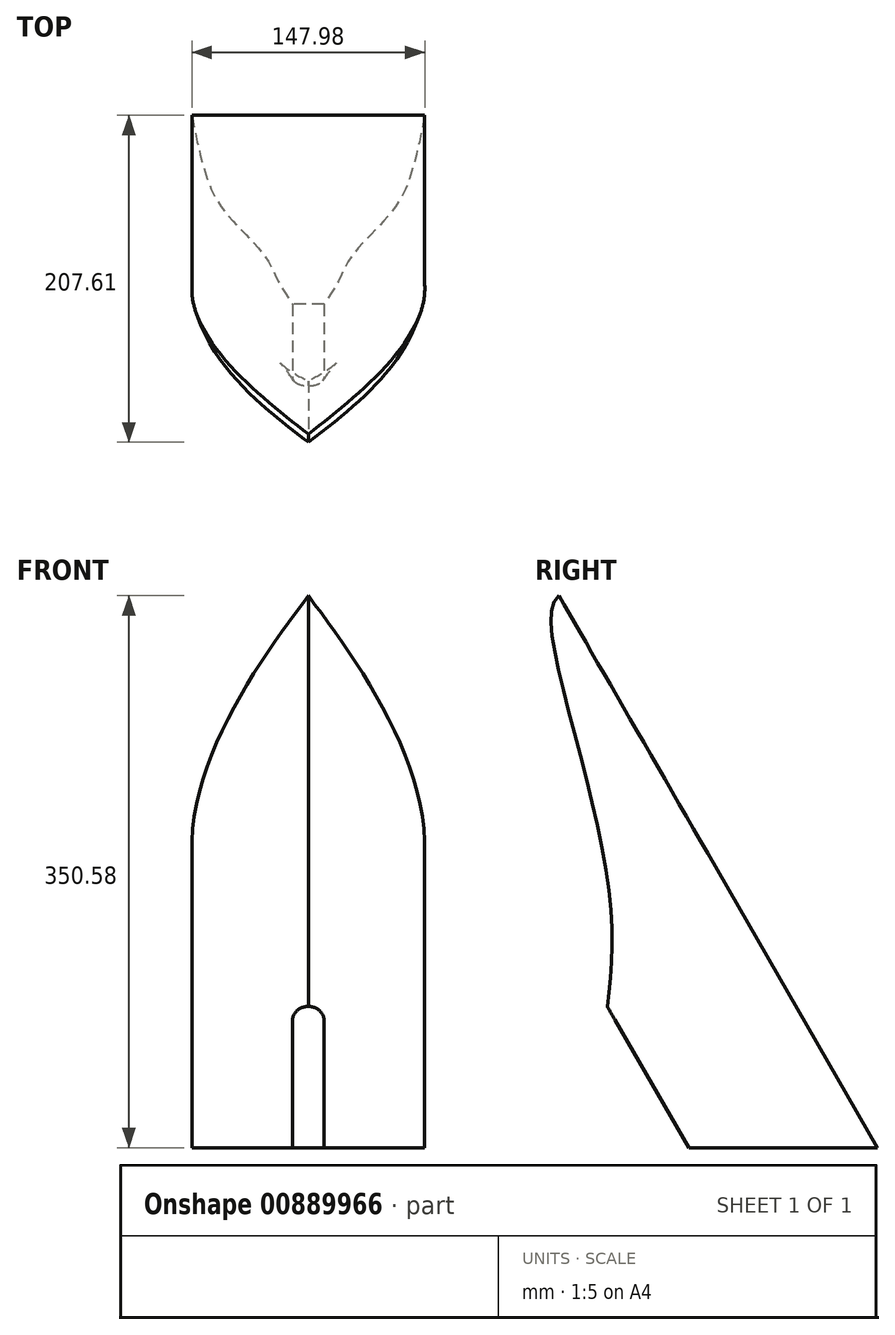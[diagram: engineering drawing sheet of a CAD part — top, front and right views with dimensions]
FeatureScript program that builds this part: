
annotation { "Feature Type Name" : "Feature", "Feature Type Description" : "" }
export const myFeature = defineFeature(function(context is Context, id is Id, definition is map)
    precondition{}
    {
        {
            var Q0;
            Q0=qCreatedBy(makeId("Top.planeOp"),FACE);
            var sketch = newSketch(context, id + "F0", { "sketchPlane" : qUnion([Q0])});
            skLineSegment(sketch, "E0", {"start": v(-73.92, 60.85) * mm, "end": v(0, 60.85) * mm});
            skPoint(sketch, "E0.startSnap0", {"position": v(0, 60.85) * mm});
            skFitSpline(sketch, "E1", {"points": [v(-73.92, 60.85) * mm, v(-60.5, 11.54) * mm, v(-42.77, -11.7) * mm, v(-25.64, -31.45) * mm, v(-18.22, -46.15) * mm, v(-9.95, -59.12) * mm], "startDerivative": vector(38.5, -196.23) * mm, "endDerivative": vector(58.27, -83.13) * mm});
            skLineSegment(sketch, "E2", {"start": v(-9.95, -59.12) * mm, "end": v(0, -59.12) * mm});
            skPoint(sketch, "E3.orphan", {"position": v(0, 0) * mm});
            skPoint(sketch, "E4.end.orphan", {"position": v(0, -90.36) * mm});
            skPoint(sketch, "E5.end.orphan", {"position": v(0, 121.7) * mm});
            skLineSegment(sketch, "E6", {"start": v(0, 100.37) * mm, "end": v(0, -90.36) * mm, "construction": true});
            skFitSpline(sketch, "E7.MirrorCS", {"points": [v(73.92, 60.85) * mm, v(60.5, 11.54) * mm, v(42.77, -11.7) * mm, v(25.64, -31.45) * mm, v(18.22, -46.15) * mm, v(9.95, -59.12) * mm], "startDerivative": vector(-38.5, -196.23) * mm, "endDerivative": vector(-58.27, -83.13) * mm});
            skLineSegment(sketch, "E8.MirrorCS", {"start": v(73.92, 60.85) * mm, "end": v(0, 60.85) * mm});
            skLineSegment(sketch, "E9.MirrorCS", {"start": v(9.95, -59.12) * mm, "end": v(0, -59.12) * mm});
            skLineSegment(sketch, "E10", {"start": v(-25.64, -31.45) * mm, "end": v(25.64, -31.45) * mm});
            skSolve(sketch);
        }
        {
            var Q0;
            Q0=sQuery(id+"F0.wireOp",EDGE,"E9.MirrorCS");
            cPlane(context, id + "F1", {"entities" : qUnion([Q0]), "cplaneType" : CPlaneType.LINE_ANGLE, "offset" : 25 * mm, "angle" : 150 * degree, "width" : 150 * mm, "height" : 150 * mm});
        }
        {
            var Q0;
            Q0=qCreatedBy(id+"F1.planeOp",FACE);
            var sketch = newSketch(context, id + "F2", { "sketchPlane" : qUnion([Q0])});
            skLineSegment(sketch, "E11.0", {"start": v(-9.95, 29.56) * mm, "end": v(0, 29.56) * mm});
            skLineSegment(sketch, "E12.0", {"start": v(9.95, 29.56) * mm, "end": v(0, 29.56) * mm});
            skLineSegment(sketch, "E13", {"start": v(-9.95, 29.56) * mm, "end": v(-9.95, 123.16) * mm});
            skLineSegment(sketch, "E14", {"start": v(9.95, 29.56) * mm, "end": v(9.95, 123.16) * mm});
            skArc(sketch, "E15", {"start": v(-9.95, 123.16) * mm, "mid": v(0, 133.11) * mm, "end": v(9.95, 123.16) * mm});
            skPoint(sketch, "E16", {"position": v(0, 133.11) * mm});
            skSolve(sketch);
        }
        {
            var Q0;
            Q0=sQuery(id+"F0.wireOp",EDGE,"E8.MirrorCS");
            cPlane(context, id + "F3", {"entities" : qUnion([Q0]), "cplaneType" : CPlaneType.LINE_ANGLE, "offset" : 25 * mm, "angle" : 150 * degree, "width" : 150 * mm, "height" : 150 * mm});
        }
        {
            var Q0;
            Q0=qCreatedBy(id+"F3.planeOp",FACE);
            var sketch = newSketch(context, id + "F4", { "sketchPlane" : qUnion([Q0])});
            skLineSegment(sketch, "E17.0", {"start": v(-73.92, -30.42) * mm, "end": v(0, -30.42) * mm});
            skLineSegment(sketch, "E18.0", {"start": v(73.92, -30.42) * mm, "end": v(0, -30.42) * mm});
            skLineSegment(sketch, "E19", {"start": v(-73.92, -30.42) * mm, "end": v(-73.92, 185.3) * mm});
            skLineSegment(sketch, "E20", {"start": v(73.92, -30.42) * mm, "end": v(73.92, 185.3) * mm});
            skFitSpline(sketch, "E21", {"points": [v(-73.92, 185.3) * mm, v(0, 374.4) * mm], "startDerivative": vector(-6.14, 208.86) * mm, "endDerivative": vector(91.46, 141.36) * mm});
            skLineSegment(sketch, "E22", {"start": v(0, -30.42) * mm, "end": v(0, 390.57) * mm, "construction": true});
            skFitSpline(sketch, "E23.MirrorCS", {"points": [v(73.92, 185.3) * mm, v(0, 374.4) * mm], "startDerivative": vector(6.14, 208.86) * mm, "endDerivative": vector(-91.46, 141.36) * mm});
            skSolve(sketch);
        }
        {
            var Q0;
            Q0=sQuery(id+"F4.wireOp",EDGE,"E22");
            cPlane(context, id + "F5", {"entities" : qUnion([Q0]), "cplaneType" : CPlaneType.LINE_ANGLE, "offset" : 25 * mm, "angle" : 0 * degree, "width" : 150 * mm, "height" : 150 * mm});
        }
        {
            var Q0;
            Q0=qCreatedBy(id+"F5.planeOp",FACE);
            var sketch = newSketch(context, id + "F6", { "sketchPlane" : qUnion([Q0])});
            skPoint(sketch, "E24.0", {"position": v(-141.56, 350.58) * mm});
            skPoint(sketch, "E25.0", {"position": v(-110.9, 89.68) * mm});
            skFitSpline(sketch, "E26", {"points": [v(-110.9, 89.68) * mm, v(-110.9, 171.43) * mm, v(-143.63, 312.22) * mm, v(-141.56, 350.58) * mm], "startDerivative": vector(28.7, 200.9) * mm, "endDerivative": vector(94.15, 70.36) * mm});
            skSolve(sketch);
        }
        {
            var Q0;
            Q0=sQuery(id+"F0.wireOp",EDGE,"E10");
            cPlane(context, id + "F7", {"entities" : qUnion([Q0]), "cplaneType" : CPlaneType.LINE_ANGLE, "offset" : 25 * mm, "angle" : 30 * degree, "width" : 150 * mm, "height" : 150 * mm});
        }
        {
            var Q0;
            Q0=qCreatedBy(id+"F7.planeOp",FACE);
            var sketch = newSketch(context, id + "F8", { "sketchPlane" : qUnion([Q0])});
            skLineSegment(sketch, "E27.0", {"start": v(25.64, 15.72) * mm, "end": v(-25.64, 15.72) * mm});
            skLineSegment(sketch, "E28", {"start": v(25.64, 15.72) * mm, "end": v(25.64, 145.02) * mm});
            skLineSegment(sketch, "E29", {"start": v(-25.64, 15.72) * mm, "end": v(-25.64, 145.02) * mm});
            skFitSpline(sketch, "E30", {"points": [v(25.64, 145.02) * mm, v(0, 168.46) * mm], "startDerivative": vector(-16.25, 29.44) * mm, "endDerivative": vector(-25.64, 22.79) * mm});
            skLineSegment(sketch, "E31", {"start": v(0, 168.46) * mm, "end": v(0, 121.19) * mm, "construction": true});
            skFitSpline(sketch, "E32.MirrorCS", {"points": [v(-25.64, 145.02) * mm, v(0, 168.46) * mm], "startDerivative": vector(16.25, 29.44) * mm, "endDerivative": vector(25.64, 22.79) * mm});
            skSolve(sketch);
        }
        {
            var Q0;
            Q0 = qSketchRegion(id + "F2", true);
            var Q1;
            Q1=makeQuery(id+"F4.imprint","IMPRINT",FACE,{"disambiguationData":[TD([[makeQuery(id+"F4.imprint","IMPRINT",EDGE,{"derivedFrom":sQuery(id+"F4.wireOp",EDGE,"E17.0")}),1.0]])]});
            var Q2;
            Q2=sQuery(id+"F0.wireOp",EDGE,"E1");
            var Q3;
            Q3=sQuery(id+"F6.wireOp",EDGE,"E26");
            var Q4;
            Q4=sQuery(id+"F0.wireOp",EDGE,"E7.MirrorCS");
            loft(context, id + "F9", {"addGuides" : true, "sheetProfilesArray" : [{ "sheetProfileEntities" : qUnion([Q0]) }, { "sheetProfileEntities" : qUnion([Q1]) }], "guidesArray" : [{ "guideEntities" : qUnion([Q2]), "guideDerivativeType" : LoftGuideDerivativeType.DEFAULT, "guideDerivativeMagnitude" : 1 }, { "guideEntities" : qUnion([Q3]), "guideDerivativeType" : LoftGuideDerivativeType.DEFAULT, "guideDerivativeMagnitude" : 1 }, { "guideEntities" : qUnion([Q4]), "guideDerivativeType" : LoftGuideDerivativeType.DEFAULT, "guideDerivativeMagnitude" : 1 }]});
        }
        {
            var Q0;
            Q0=makeQuery(id+"F9.opLoft","CAP_FACE",FACE,{"disambiguationData":[OSD([makeQuery(id+"F2.imprint","IMPRINT",FACE,{"disambiguationData":[TD([[makeQuery(id+"F2.imprint","IMPRINT",EDGE,{"derivedFrom":sQuery(id+"F2.wireOp",EDGE,"E11.0")}),1.0]])]})])],"isStart":true});
            cPlane(context, id + "F10", {"entities" : qUnion([Q0]), "cplaneType" : CPlaneType.OFFSET, "offset" : 15 * mm, "width" : 150 * mm, "height" : 150 * mm});
        }
    });
